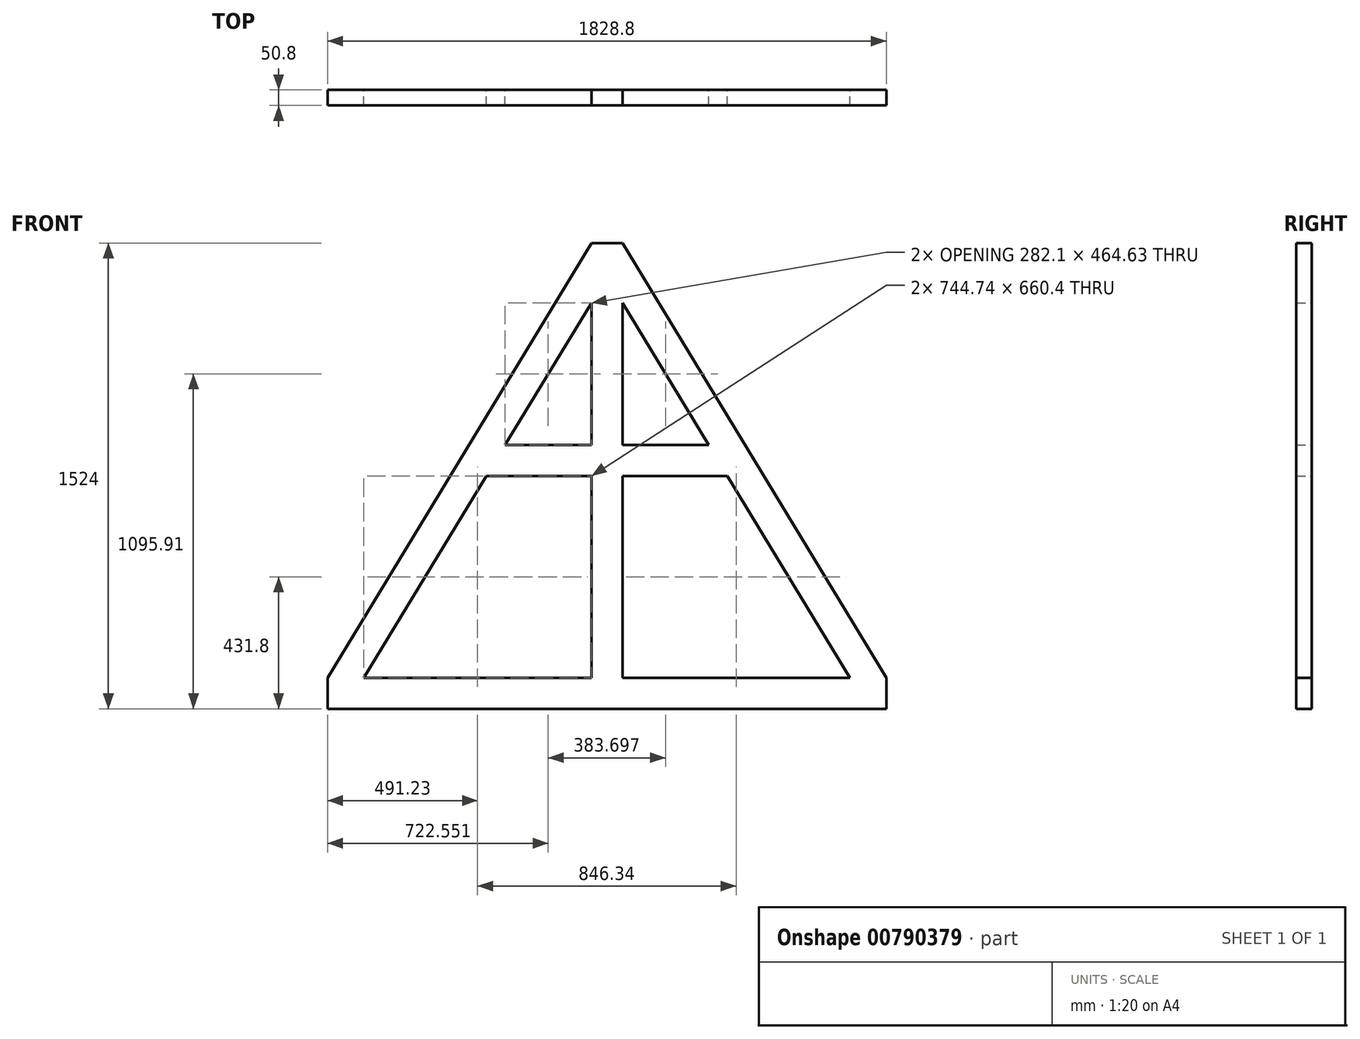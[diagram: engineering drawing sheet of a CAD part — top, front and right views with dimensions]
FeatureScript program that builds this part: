
annotation { "Feature Type Name" : "Feature", "Feature Type Description" : "" }
export const myFeature = defineFeature(function(context is Context, id is Id, definition is map)
    precondition{}
    {
        {
            var Q0;
            Q0=qCreatedBy(makeId("Front.planeOp"),FACE);
            var sketch = newSketch(context, id + "F0", { "sketchPlane" : qUnion([Q0])});
            skLineSegment(sketch, "E0.bottom", {"start": v(0, 0) * mm, "end": v(101.6, 0) * mm});
            skLineSegment(sketch, "E0.top", {"start": v(0, 1524) * mm, "end": v(101.6, 1524) * mm});
            skLineSegment(sketch, "E0.left", {"start": v(0, 0) * mm, "end": v(0, 1524) * mm});
            skLineSegment(sketch, "E0.right", {"start": v(101.6, 0) * mm, "end": v(101.6, 1524) * mm});
            skSolve(sketch);
        }
        {
            var Q0;
            Q0=makeQuery(id+"F0.imprint","IMPRINT",FACE,{"disambiguationData":[TD([[makeQuery(id+"F0.imprint","IMPRINT",EDGE,{"derivedFrom":sQuery(id+"F0.wireOp",EDGE,"E0.bottom")}),1.0]])]});
            extrude(context, id + "F1", {"entities" : qUnion([Q0]), "depth" : 50.8 * mm, "offsetDistance" : 25.4 * mm});
        }
        {
            var Q0;
            Q0=qCreatedBy(makeId("Front.planeOp"),FACE);
            var sketch = newSketch(context, id + "F2", { "sketchPlane" : qUnion([Q0])});
            skLineSegment(sketch, "E1", {"start": v(50.8, 0) * mm, "end": v(-863.6, 0) * mm});
            skLineSegment(sketch, "E2", {"start": v(-863.6, 0) * mm, "end": v(-863.6, 101.6) * mm});
            skLineSegment(sketch, "E3", {"start": v(-863.6, 101.6) * mm, "end": v(0, 1524) * mm});
            skLineSegment(sketch, "E4", {"start": v(0, 1328.23) * mm, "end": v(-744.74, 101.6) * mm});
            skLineSegment(sketch, "E5", {"start": v(-744.74, 101.6) * mm, "end": v(-863.6, 101.6) * mm});
            skLineSegment(sketch, "E6", {"start": v(0, 1524) * mm, "end": v(0, 1328.23) * mm});
            skLineSegment(sketch, "E7", {"start": v(-744.74, 101.6) * mm, "end": v(0, 101.6) * mm});
            skLineSegment(sketch, "E8", {"start": v(0, 101.6) * mm, "end": v(0, 0) * mm});
            skLineSegment(sketch, "E9", {"start": v(50.8, 0) * mm, "end": v(50.8, 1581.75) * mm});
            skLineSegment(sketch, "E10.MirrorCS", {"start": v(101.6, 1328.23) * mm, "end": v(846.34, 101.6) * mm});
            skLineSegment(sketch, "E11.MirrorCS", {"start": v(101.6, 1524) * mm, "end": v(101.6, 1328.23) * mm});
            skLineSegment(sketch, "E12.MirrorCS", {"start": v(965.2, 101.6) * mm, "end": v(101.6, 1524) * mm});
            skLineSegment(sketch, "E13.MirrorCS", {"start": v(846.34, 101.6) * mm, "end": v(965.2, 101.6) * mm});
            skLineSegment(sketch, "E14.MirrorCS", {"start": v(965.2, 0) * mm, "end": v(965.2, 101.6) * mm});
            skLineSegment(sketch, "E15.MirrorCS", {"start": v(50.8, 0) * mm, "end": v(965.2, 0) * mm});
            skLineSegment(sketch, "E16.MirrorCS", {"start": v(846.34, 101.6) * mm, "end": v(101.6, 101.6) * mm});
            skLineSegment(sketch, "E17.MirrorCS", {"start": v(101.6, 101.6) * mm, "end": v(101.6, 0) * mm});
            skSolve(sketch);
        }
        {
            var Q0;
            Q0=makeQuery(id+"F2.imprint","IMPRINT",FACE,{"disambiguationData":[TD([[makeQuery(id+"F2.imprint","IMPRINT",EDGE,{"derivedFrom":sQuery(id+"F2.wireOp",EDGE,"E3")}),-1.0]])]});
            var Q1;
            {var subQ0=sQuery(id+"F2.wireOp",EDGE,"E2");Q1=makeQuery(id+"F2.imprint","IMPRINT",FACE,{"disambiguationData":[TD([[makeQuery(id+"F2.imprint","IMPRINT",EDGE,{"derivedFrom":subQ0}),-1.0]])]});}
            var Q2;
            Q2=makeQuery(id+"F2.imprint","IMPRINT",FACE,{"disambiguationData":[TD([[makeQuery(id+"F2.imprint","IMPRINT",EDGE,{"derivedFrom":sQuery(id+"F2.wireOp",EDGE,"E13.MirrorCS")}),-1.0]])]});
            var Q3;
            Q3=makeQuery(id+"F2.imprint","IMPRINT",FACE,{"disambiguationData":[TD([[makeQuery(id+"F2.imprint","IMPRINT",EDGE,{"derivedFrom":sQuery(id+"F2.wireOp",EDGE,"E10.MirrorCS")}),1.0]])]});
            extrude(context, id + "F3", {"entities" : qUnion([Q0, Q1, Q2, Q3]), "operationType" : NewBodyOperationType.ADD, "depth" : 50.8 * mm, "offsetDistance" : 25.4 * mm});
        }
        {
            var Q0;
            Q0=qCreatedBy(makeId("Front.planeOp"),FACE);
            var sketch = newSketch(context, id + "F4", { "sketchPlane" : qUnion([Q0])});
            skLineSegment(sketch, "E18", {"start": v(0, 762) * mm, "end": v(-343.78, 762) * mm});
            skLineSegment(sketch, "E19", {"start": v(-343.78, 762) * mm, "end": v(-282.1, 863.6) * mm});
            skLineSegment(sketch, "E20", {"start": v(-282.1, 863.6) * mm, "end": v(0, 863.6) * mm});
            skLineSegment(sketch, "E21", {"start": v(0, 863.6) * mm, "end": v(0, 762) * mm});
            skLineSegment(sketch, "E22", {"start": v(101.6, 863.6) * mm, "end": v(383.7, 863.6) * mm});
            skLineSegment(sketch, "E23", {"start": v(383.7, 863.6) * mm, "end": v(445.38, 762) * mm});
            skLineSegment(sketch, "E24", {"start": v(445.38, 762) * mm, "end": v(101.6, 762) * mm});
            skLineSegment(sketch, "E25", {"start": v(101.6, 762) * mm, "end": v(101.6, 863.6) * mm});
            skSolve(sketch);
        }
        {
            var Q0;
            Q0=makeQuery(id+"F4.imprint","IMPRINT",FACE,{"disambiguationData":[TD([[makeQuery(id+"F4.imprint","IMPRINT",EDGE,{"derivedFrom":sQuery(id+"F4.wireOp",EDGE,"E18")}),-1.0]])]});
            var Q1;
            Q1=makeQuery(id+"F4.imprint","IMPRINT",FACE,{"disambiguationData":[TD([[makeQuery(id+"F4.imprint","IMPRINT",EDGE,{"derivedFrom":sQuery(id+"F4.wireOp",EDGE,"E22")}),-1.0]])]});
            extrude(context, id + "F5", {"entities" : qUnion([Q0, Q1]), "operationType" : NewBodyOperationType.ADD, "depth" : 50.8 * mm, "offsetDistance" : 25.4 * mm});
        }
    });
